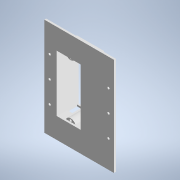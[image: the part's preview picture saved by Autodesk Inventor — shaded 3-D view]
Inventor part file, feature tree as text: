
AUTODESK INVENTOR PART (.ipt)
format: ipt  version: 2022 (Build 260153000, 153)  size: 160,256 bytes
history: native  units: mm
features: reference x10, other x5, extrude x4, sketch x4
ambient origin geometry x8: Origin, YZ Plane, XZ Plane, XY Plane, X Axis, Y Axis, Z Axis, Center Point
bodies: Body1 (feature_tree)
feature tree (23):
  other  "Твердое тело1"
  extrude  "Выдавливание1"  Depth=50.0mm
  extrude  "Выдавливание2"  Depth=110.0mm
  extrude  "Выдавливание3"  Depth=180.0mm
  extrude  "Выдавливание4"  Depth=35.0mm
  sketch  "Эскиз1"
  reference  "Ссылка1"
  reference  "Ссылка2"
  reference  "Ссылка3"
  reference  "Ссылка4"
  reference  "Ссылка5"
  reference  "Ссылка6"
  reference  "Ссылка7"
  reference  "Ссылка8"
  reference  "Ссылка9"
  reference  "Ссылка10"
  sketch  "Эскиз2"
  sketch  "Эскиз3"
  sketch  "Эскиз4"
  other  "<path> - Robot.iam"
  other  "000.000 - Robot.iam"
  other  "000.002 - bamper:1"
  other  "rpi3-bottom:1"
note: 1 file-system path scrubbed to <path> (originals preserved in map.json)
